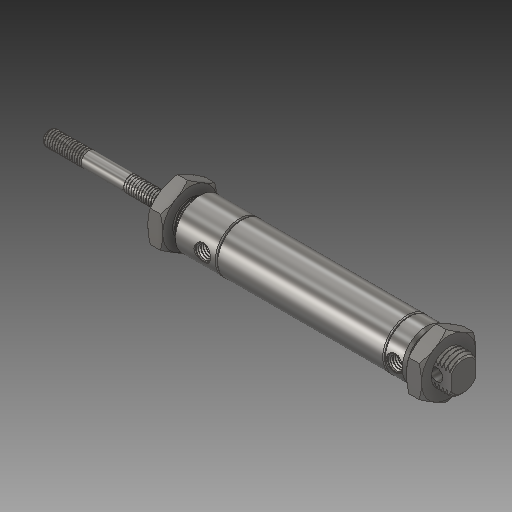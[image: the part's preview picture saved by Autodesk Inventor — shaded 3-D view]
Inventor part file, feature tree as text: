
AUTODESK INVENTOR PART (.ipt)
format: ipt  version: 2018 (Build 220112000, 112)  size: 1,796,608 bytes
history: native  units: in
note: dims shown in document units (in); Inventor stores cm internally (conversion verified against a paired STEP export)
features: other x3, revolve x1, boolean_combine x1
ambient origin geometry x8: Origin, YZ Plane, XZ Plane, XY Plane, X Axis, Y Axis, Z Axis, Center Point
bodies: Solid1 (feature_tree), Solid2 (feature_tree), Solid3 (feature_tree), Solid4 (feature_tree), Solid5 (feature_tree)
feature tree (5):
  other  "Cut-Extrude4"
  revolve  "Revolve4"  [1 undecoded]
  other  "Body-Move_Copy3"
  other  "Cut-Extrude8"
  boolean_combine  "Combine6"
note: 1 required parameter value undecoded (feature->parameter linkage not recoverable at this tier; creation-order binding heuristic only, values carry confidence <= 0.55)
